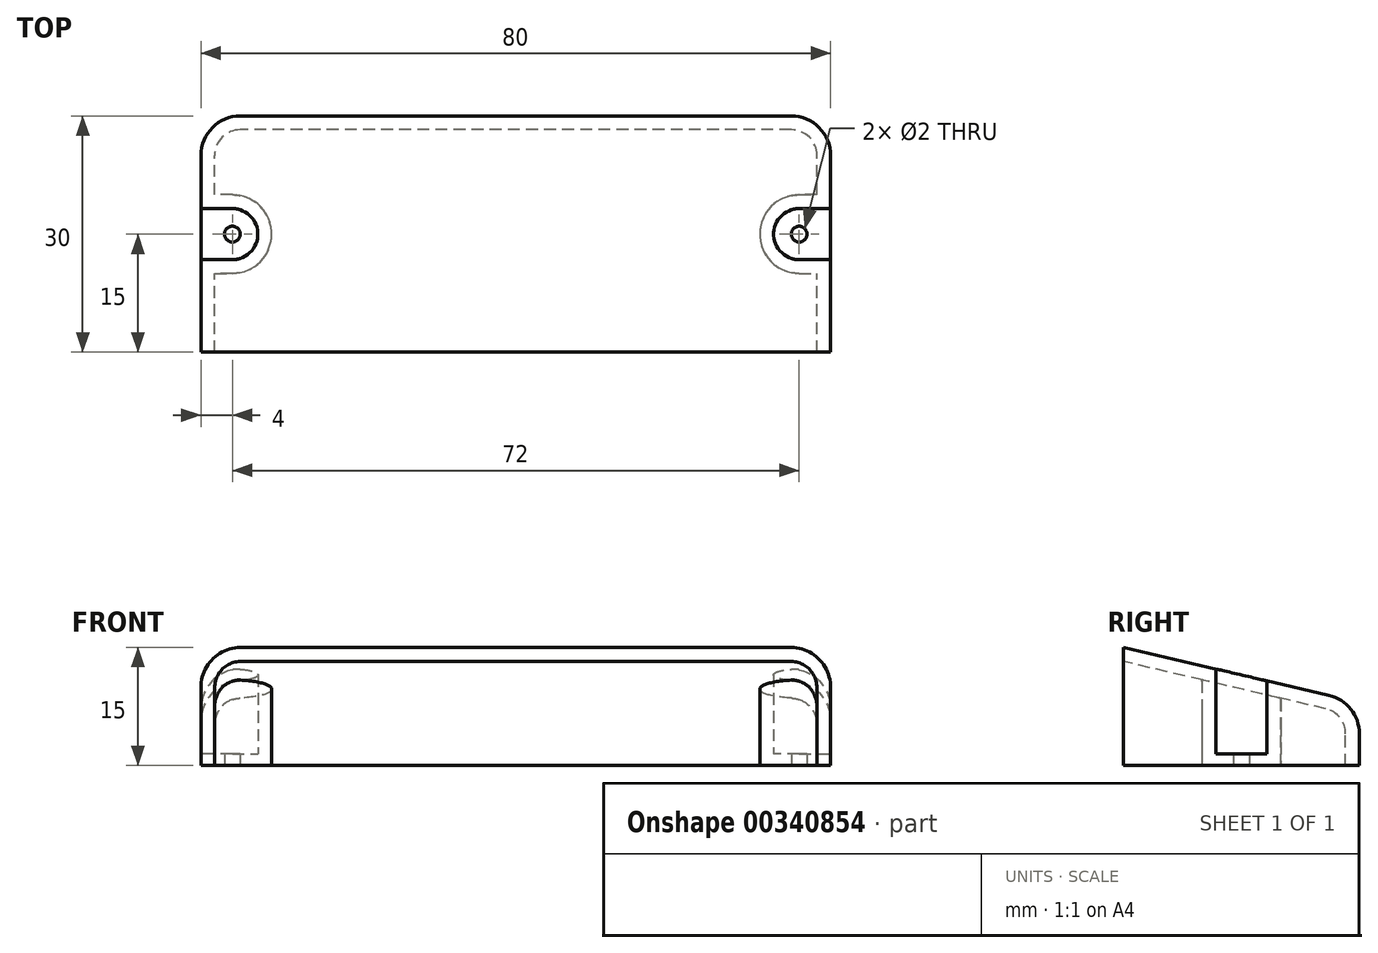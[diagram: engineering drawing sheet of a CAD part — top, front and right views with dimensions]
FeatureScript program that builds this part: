
annotation { "Feature Type Name" : "Feature", "Feature Type Description" : "" }
export const myFeature = defineFeature(function(context is Context, id is Id, definition is map)
    precondition{}
    {
        {
            var Q0;
            Q0=qCreatedBy(makeId("Right.planeOp"),FACE);
            var sketch = newSketch(context, id + "F0", { "sketchPlane" : qUnion([Q0])});
            skLineSegment(sketch, "E0.bottom", {"start": v(-15, 0) * mm, "end": v(15, 0) * mm});
            skLineSegment(sketch, "E1", {"start": v(-15, 0) * mm, "end": v(-15, 15) * mm});
            skLineSegment(sketch, "E2", {"start": v(-15, 15) * mm, "end": v(15, 8) * mm});
            skLineSegment(sketch, "E3", {"start": v(15, 8) * mm, "end": v(15, 0) * mm});
            skLineSegment(sketch, "E4", {"start": v(0, -56.66) * mm, "end": v(0, 58.83) * mm, "construction": true});
            skSolve(sketch);
        }
        {
            var Q0;
            Q0=qSketchRegion(id+"F0",true);
            extrude(context, id + "F1", {"entities" : qUnion([Q0]), "depth" : 40 * mm, "hasSecondDirection" : true, "secondDirectionOppositeDirection" : true, "secondDirectionDepth" : 40 * mm});
        }
        {
            var Q0;
            Q0=makeQuery(id+"F1.opExtrude","CAP_EDGE",EDGE,{"disambiguationData":[OSD([sQuery(id+"F0.wireOp",EDGE,"E2")])],"isStart":false});
            var Q1;
            Q1=makeQuery(id+"F1.opExtrude","CAP_EDGE",EDGE,{"disambiguationData":[OSD([sQuery(id+"F0.wireOp",EDGE,"E2")])],"isStart":true});
            var Q2;
            Q2=makeQuery(id+"F1.opExtrude","SWEPT_EDGE",EDGE,{"disambiguationData":[OSD([sQuery(id+"F0.wireOp",EDGE,"E2"),sQuery(id+"F0.wireOp",EDGE,"E3")])]});
            var Q3;
            Q3=makeQuery(id+"F1.opExtrude","CAP_EDGE",EDGE,{"disambiguationData":[OSD([sQuery(id+"F0.wireOp",EDGE,"E3")])],"isStart":false});
            var Q4;
            Q4=makeQuery(id+"F1.opExtrude","CAP_EDGE",EDGE,{"disambiguationData":[OSD([sQuery(id+"F0.wireOp",EDGE,"E3")])],"isStart":true});
            fillet(context, id + "F2", {"entities" : qUnion([Q0, Q1, Q2, Q3, Q4]), "radius" : 5 * mm, "tangentPropagation" : true, "allowEdgeOverflow" : false});
        }
        {
            var Q0;
            Q0=qCreatedBy(makeId("Top.planeOp"),FACE);
            var sketch = newSketch(context, id + "F3", { "sketchPlane" : qUnion([Q0])});
            skCircle(sketch, "E5", {"center": v(-36, 0) * mm, "radius": 1 * mm});
            skCircle(sketch, "E6", {"center": v(36, 0) * mm, "radius": 1 * mm});
            skLineSegment(sketch, "E7", {"start": v(0, -59.31) * mm, "end": v(0, 47.59) * mm, "construction": true});
            skSolve(sketch);
        }
        {
            var Q0;
            Q0=qSketchRegion(id+"F3",true);
            extrude(context, id + "F4", {"entities" : qUnion([Q0]), "operationType" : NewBodyOperationType.REMOVE, "depth" : 39 * mm});
        }
        {
            var Q0;
            Q0=qCreatedBy(makeId("Top.planeOp"),FACE);
            cPlane(context, id + "F5", {"entities" : qUnion([Q0]), "cplaneType" : CPlaneType.OFFSET, "offset" : 1.5 * mm, "width" : 150 * mm, "height" : 150 * mm});
        }
        {
            var Q0;
            Q0=qCreatedBy(id+"F5.planeOp",FACE);
            var sketch = newSketch(context, id + "F6", { "sketchPlane" : qUnion([Q0])});
            skArc(sketch, "E8", {"start": v(-36, -3.25) * mm, "mid": v(-32.75, 0) * mm, "end": v(-36, 3.25) * mm});
            skLineSegment(sketch, "E9.bottom", {"start": v(-36, 3.25) * mm, "end": v(-40, 3.25) * mm});
            skLineSegment(sketch, "E9.top", {"start": v(-36, -3.25) * mm, "end": v(-40, -3.25) * mm});
            skLineSegment(sketch, "E9.right", {"start": v(-40, 3.25) * mm, "end": v(-40, -3.25) * mm});
            skLineSegment(sketch, "E10", {"start": v(0, -51.5) * mm, "end": v(0, 51.02) * mm, "construction": true});
            skLineSegment(sketch, "E11.MirrorCS", {"start": v(36, 3.25) * mm, "end": v(40, 3.25) * mm});
            skArc(sketch, "E12.MirrorCS", {"start": v(36, -3.25) * mm, "mid": v(32.75, 0) * mm, "end": v(36, 3.25) * mm});
            skLineSegment(sketch, "E13.MirrorCS", {"start": v(36, -3.25) * mm, "end": v(40, -3.25) * mm});
            skLineSegment(sketch, "E14.MirrorCS", {"start": v(40, 3.25) * mm, "end": v(40, -3.25) * mm});
            skSolve(sketch);
        }
        {
            var Q0;
            Q0=qSketchRegion(id+"F6",true);
            extrude(context, id + "F7", {"entities" : qUnion([Q0]), "operationType" : NewBodyOperationType.REMOVE, "depth" : 25 * mm});
        }
        {
            var Q0;
            Q0=makeQuery(id+"F1.opExtrude","SWEPT_FACE",FACE,{"disambiguationData":[OSD([sQuery(id+"F0.wireOp",EDGE,"E0.bottom")])]});
            var Q1;
            Q1=makeQuery(id+"F1.opExtrude","SWEPT_FACE",FACE,{"disambiguationData":[OSD([sQuery(id+"F0.wireOp",EDGE,"E1")])]});
            shell(context, id + "F8", {"entities" : qUnion([Q0, Q1]), "thickness" : 1.75 * mm});
        }
    });
